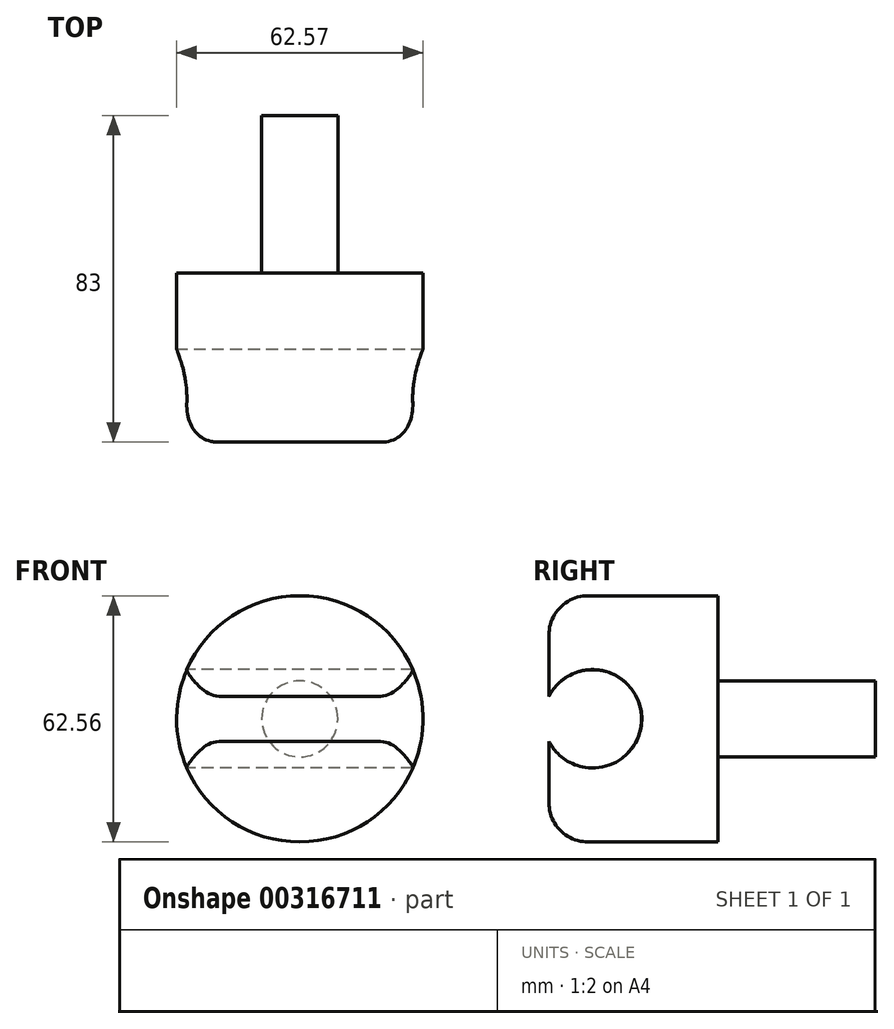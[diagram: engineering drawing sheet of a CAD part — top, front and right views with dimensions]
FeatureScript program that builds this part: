
annotation { "Feature Type Name" : "Feature", "Feature Type Description" : "" }
export const myFeature = defineFeature(function(context is Context, id is Id, definition is map)
    precondition{}
    {
        {
            var Q0;
            Q0=qCreatedBy(makeId("Front.planeOp"),FACE);
            var sketch = newSketch(context, id + "F0", { "sketchPlane" : qUnion([Q0])});
            skCircle(sketch, "E0", {"center": v(3, 0) * mm, "radius": 31.28 * mm});
            skSolve(sketch);
        }
        {
            var Q0;
            Q0=makeQuery(id+"F0.imprint","IMPRINT",FACE,{"disambiguationData":[TD([[makeQuery(id+"F0.imprint","IMPRINT",EDGE,{"derivedFrom":sQuery(id+"F0.wireOp",EDGE,"E0")}),1.0]])]});
            extrude(context, id + "F1", {"entities" : qUnion([Q0]), "depth" : 43 * mm});
        }
        {
            var Q0;
            Q0=qCreatedBy(makeId("Right.planeOp"),FACE);
            var sketch = newSketch(context, id + "F2", { "sketchPlane" : qUnion([Q0])});
            skCircle(sketch, "E1", {"center": v(-31.9, 0) * mm, "radius": 12.5 * mm});
            skSolve(sketch);
        }
        {
            var Q0;
            Q0=makeQuery(id+"F2.imprint","IMPRINT",FACE,{"disambiguationData":[TD([[makeQuery(id+"F2.imprint","IMPRINT",EDGE,{"derivedFrom":sQuery(id+"F2.wireOp",EDGE,"E1")}),1.0]])]});
            extrude(context, id + "F3", {"entities" : qUnion([Q0]), "operationType" : NewBodyOperationType.REMOVE, "endBound" : BoundingType.SYMMETRIC, "depth" : 80 * mm});
        }
        {
            var Q0;
            Q0=makeQuery(id+"F3.boolean.opBoolean","SPLIT",EDGE,{"disambiguationData":[OD(1.0)],"derivedFrom":makeQuery(id+"F1.opExtrude","CAP_EDGE",EDGE,{"disambiguationData":[OSD([sQuery(id+"F0.wireOp",EDGE,"E0")])],"isStart":false})});
            var Q1;
            Q1=makeQuery(id+"F3.boolean.opBoolean","SPLIT",EDGE,{"disambiguationData":[OD(0.0)],"derivedFrom":makeQuery(id+"F1.opExtrude","CAP_EDGE",EDGE,{"disambiguationData":[OSD([sQuery(id+"F0.wireOp",EDGE,"E0")])],"isStart":false})});
            fillet(context, id + "F4", {"entities" : qUnion([Q0, Q1]), "radius" : 10 * mm, "tangentPropagation" : true, "allowEdgeOverflow" : false});
        }
        {
            var Q0;
            Q0=makeQuery(id+"F1.opExtrude","CAP_FACE",FACE,{"disambiguationData":[OSD([sQuery(id+"F0.wireOp",EDGE,"E0")])],"isStart":true});
            var sketch = newSketch(context, id + "F5", { "sketchPlane" : qUnion([Q0])});
            skCircle(sketch, "E2", {"center": v(-3, 0) * mm, "radius": 9.67 * mm});
            skSolve(sketch);
        }
        {
            var Q0;
            Q0=makeQuery(id+"F5.imprint","IMPRINT",FACE,{"disambiguationData":[TD([[makeQuery(id+"F5.imprint","IMPRINT",EDGE,{"derivedFrom":sQuery(id+"F5.wireOp",EDGE,"E2")}),1.0]])]});
            extrude(context, id + "F6", {"entities" : qUnion([Q0]), "operationType" : NewBodyOperationType.ADD, "depth" : 40 * mm});
        }
    });
